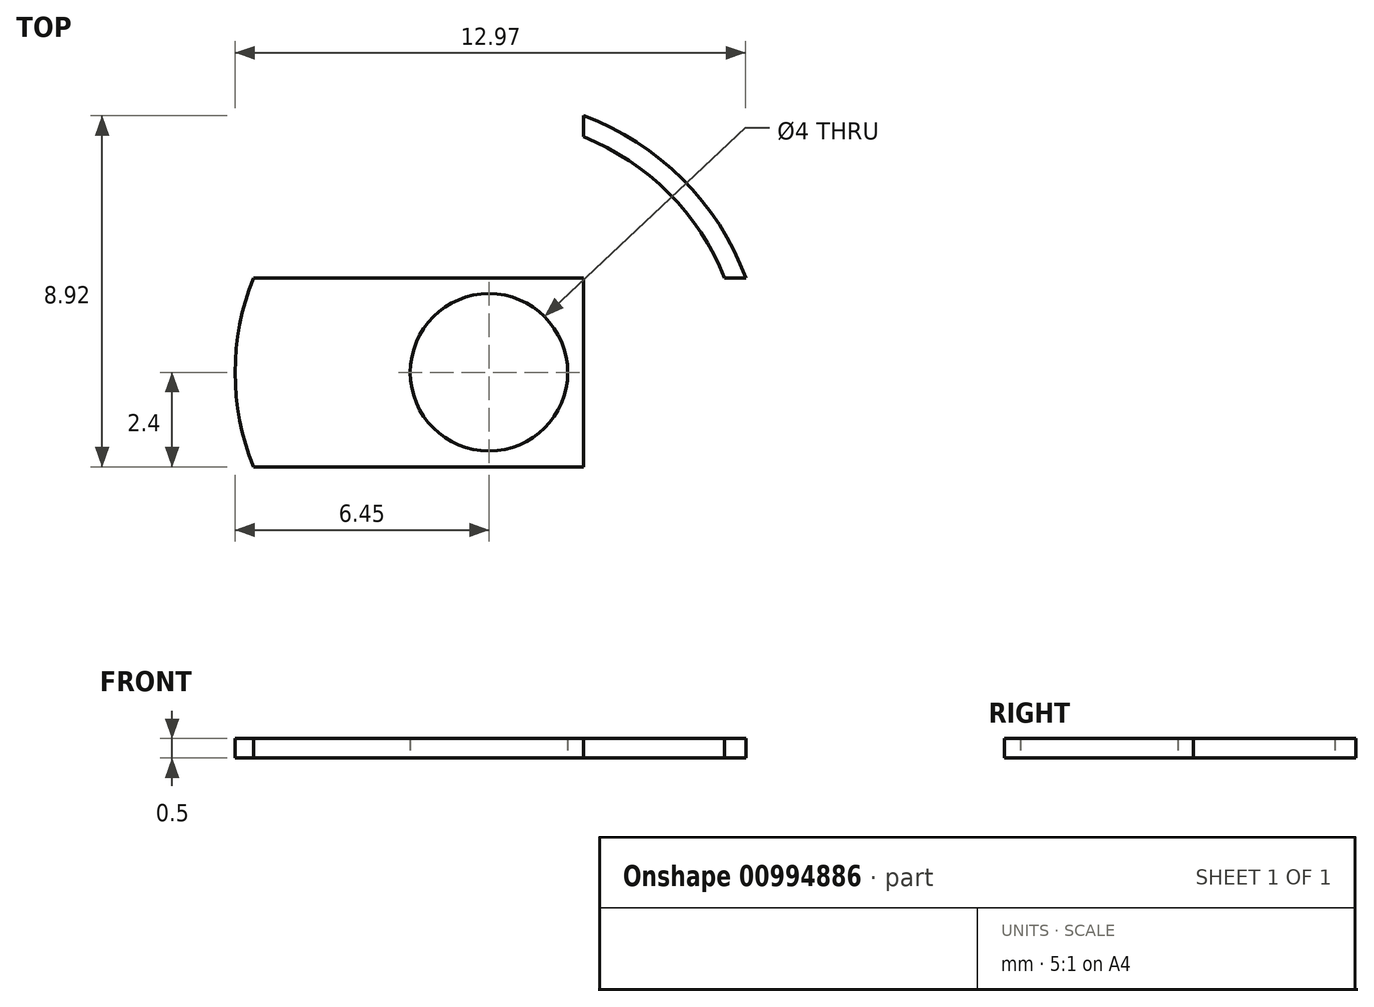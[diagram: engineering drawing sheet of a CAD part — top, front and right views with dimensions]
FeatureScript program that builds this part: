
annotation { "Feature Type Name" : "Feature", "Feature Type Description" : "" }
export const myFeature = defineFeature(function(context is Context, id is Id, definition is map)
    precondition{}
    {
        {
            var Q0;
            Q0=qCreatedBy(makeId("Top.planeOp"),FACE);
            var sketch = newSketch(context, id + "F0", { "sketchPlane" : qUnion([Q0])});
            skCircle(sketch, "E0", {"center": v(0, 0) * mm, "radius": 6.95 * mm});
            skCircle(sketch, "E1", {"center": v(0, 0) * mm, "radius": 2 * mm});
            skCircle(sketch, "E2", {"center": v(0, 0) * mm, "radius": 6.45 * mm});
            skLineSegment(sketch, "E3", {"start": v(-6.52, 2.4) * mm, "end": v(6.52, 2.4) * mm});
            skLineSegment(sketch, "E4", {"start": v(-6.52, -2.4) * mm, "end": v(6.52, -2.4) * mm});
            skLineSegment(sketch, "E5", {"start": v(2.4, 6.52) * mm, "end": v(2.4, -6.52) * mm});
            skSolve(sketch);
        }
        {
            var Q0;
            {var subQ0=sQuery(id+"F0.wireOp",EDGE,"E3");var subQ1=sQuery(id+"F0.wireOp",EDGE,"E0");var subQ2=makeQuery(id+"F0.imprint","INTERSECT",VERTEX,{"disambiguationData":[OD(0.0)],"derivedFrom":[subQ1,subQ0]});Q0=makeQuery(id+"F0.imprint","IMPRINT",FACE,{"disambiguationData":[TD([[makeQuery(id+"F0.imprint","IMPRINT",EDGE,{"disambiguationData":[TD([[subQ2,-1.0]])],"derivedFrom":subQ1}),1.0]])]});}
            var Q1;
            Q1=makeQuery(id+"F0.imprint","IMPRINT",FACE,{"disambiguationData":[TD([[makeQuery(id+"F0.imprint","IMPRINT",EDGE,{"derivedFrom":sQuery(id+"F0.wireOp",EDGE,"E1")}),-1.0]])]});
            extrude(context, id + "F1", {"entities" : qUnion([Q0, Q1]), "depth" : .5 * mm, "offsetDistance" : 25 * mm});
        }
    });
